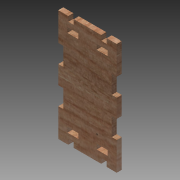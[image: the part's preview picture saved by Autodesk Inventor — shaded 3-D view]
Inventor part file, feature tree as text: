
AUTODESK INVENTOR PART (.ipt)
format: ipt  version: 2015 (Build 190159000, 159)  size: 327,680 bytes
history: native  units: mm
features: other x10, sketch x6, extrude x4
ambient origin geometry x8: Origin, YZ Plane, XZ Plane, XY Plane, X Axis, Y Axis, Z Axis, Center Point
bodies: Solid1 (feature_tree)
feature tree (20):
  other  "Blocks"
  extrude  "Extrusion1"  Depth=100.0mm
  extrude  "Extrusion3"  TaperAngle=0.0deg  [1 undecoded]
  extrude  "Extrusion4"  Depth=20.0mm
  extrude  "Extrusion7"  Depth=5.5mm
  sketch  "Sketch15"  dims[d16=0.0mm]
  sketch  "Sketch16"  dims[d17=5.5mm d18=12.0mm d19=20.0mm d20=5.5mm d21=0.0mm d22=11.0mm d23=6.0mm d24=5.5mm d32=15.0mm d33=5.5mm d34=0.0mm d55=64.0mm]
  other  "Kerf0.1"
  sketch  "Sketch1"  dims[d0=64.0mm d1=100.0mm]
  sketch  "Sketch5"  dims[d2=5.5mm d3=0.0mm]
  sketch  "Sketch6"  dims[d12=20.0mm d13=20.0mm]
  sketch  "Sketch7"  dims[d14=5.5mm d15=5.5mm]
  other  "Block1"
  other  "Block2"
  other  "Block3"
  other  "Block4"
  other  "Block3:1"
  other  "Block3:2"
  other  "Block4:1"
  other  "Block4:2"
note: 1 required parameter value undecoded (feature->parameter linkage not recoverable at this tier; creation-order binding heuristic only, values carry confidence <= 0.55)
